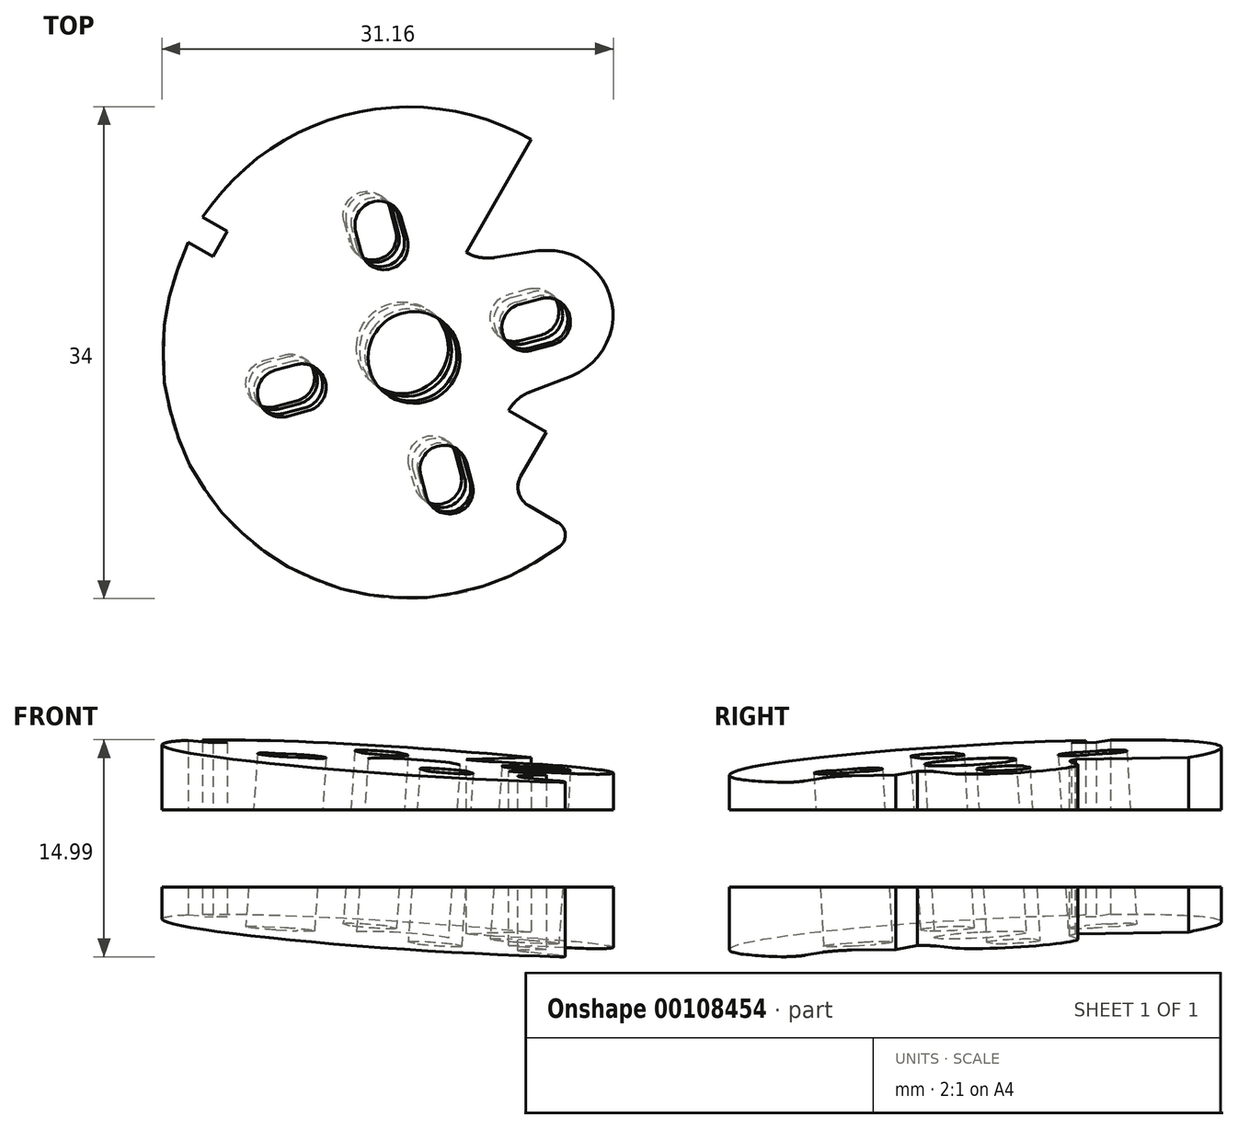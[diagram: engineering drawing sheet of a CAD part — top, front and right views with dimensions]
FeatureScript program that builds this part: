
annotation { "Feature Type Name" : "Feature", "Feature Type Description" : "" }
export const myFeature = defineFeature(function(context is Context, id is Id, definition is map)
    precondition{}
    {
        {
            var Q0;
            Q0=qCreatedBy(makeId("Top.planeOp"),FACE);
            var sketch = newSketch(context, id + "F0", { "sketchPlane" : qUnion([Q0])});
            skCircle(sketch, "E0", {"center": v(0, 0) * mm, "radius": 17 * mm});
            skLineSegment(sketch, "E1", {"start": v(10.93, 13.02) * mm, "end": v(-10.93, -13.02) * mm, "construction": true});
            skSolve(sketch);
        }
        {
            var Q0;
            Q0=qCreatedBy(makeId("Top.planeOp"),FACE);
            var sketch = newSketch(context, id + "F1", { "sketchPlane" : qUnion([Q0])});
            skLineSegment(sketch, "E2", {"start": v(-8.5, -14.72) * mm, "end": v(8.5, 14.72) * mm, "construction": true});
            skPoint(sketch, "E3", {"position": v(0, 0) * mm});
            skLineSegment(sketch, "E4", {"start": v(0, 0) * mm, "end": v(9.18, 2.46) * mm, "construction": true});
            skPoint(sketch, "E5", {"position": v(7.73, 2.07) * mm});
            skArc(sketch, "E6", {"start": v(9.6, 0.91) * mm, "mid": v(10.72, 2.87) * mm, "end": v(8.76, 4) * mm, "construction": true});
            skArc(sketch, "E7", {"start": v(7.31, 3.62) * mm, "mid": v(6.18, 1.66) * mm, "end": v(8.14, 0.53) * mm, "construction": true});
            skLineSegment(sketch, "E8", {"start": v(8.76, 4) * mm, "end": v(7.31, 3.62) * mm, "construction": true});
            skLineSegment(sketch, "E9", {"start": v(9.6, 0.91) * mm, "end": v(8.14, 0.53) * mm, "construction": true});
            skLineSegment(sketch, "E10.1.0", {"start": v(-4, 8.76) * mm, "end": v(-3.62, 7.31) * mm, "construction": true});
            skLineSegment(sketch, "E10.1.1", {"start": v(-0.91, 9.6) * mm, "end": v(-0.53, 8.14) * mm, "construction": true});
            skArc(sketch, "E10.1.2", {"start": v(-3.62, 7.31) * mm, "mid": v(-1.66, 6.18) * mm, "end": v(-0.53, 8.14) * mm, "construction": true});
            skArc(sketch, "E10.1.3", {"start": v(-0.91, 9.6) * mm, "mid": v(-2.87, 10.72) * mm, "end": v(-4, 8.76) * mm, "construction": true});
            skPoint(sketch, "E10.1.4", {"position": v(-2.07, 7.73) * mm});
            skLineSegment(sketch, "E10.2.0", {"start": v(-8.76, -4) * mm, "end": v(-7.31, -3.62) * mm, "construction": true});
            skLineSegment(sketch, "E10.2.1", {"start": v(-9.6, -0.91) * mm, "end": v(-8.14, -0.53) * mm, "construction": true});
            skArc(sketch, "E10.2.2", {"start": v(-7.31, -3.62) * mm, "mid": v(-6.18, -1.66) * mm, "end": v(-8.14, -0.53) * mm, "construction": true});
            skArc(sketch, "E10.2.3", {"start": v(-9.6, -0.91) * mm, "mid": v(-10.72, -2.87) * mm, "end": v(-8.76, -4) * mm, "construction": true});
            skPoint(sketch, "E10.2.4", {"position": v(-7.73, -2.07) * mm});
            skLineSegment(sketch, "E10.3.0", {"start": v(4, -8.76) * mm, "end": v(3.62, -7.31) * mm, "construction": true});
            skLineSegment(sketch, "E10.3.1", {"start": v(0.91, -9.6) * mm, "end": v(0.53, -8.14) * mm, "construction": true});
            skArc(sketch, "E10.3.2", {"start": v(3.62, -7.31) * mm, "mid": v(1.66, -6.18) * mm, "end": v(0.53, -8.14) * mm, "construction": true});
            skArc(sketch, "E10.3.3", {"start": v(0.91, -9.6) * mm, "mid": v(2.87, -10.72) * mm, "end": v(4, -8.76) * mm, "construction": true});
            skPoint(sketch, "E10.3.4", {"position": v(2.07, -7.73) * mm});
            skSolve(sketch);
        }
        {
            var Q0;
            Q0=sQuery(id+"F0.wireOp",EDGE,"E1");
            cPlane(context, id + "F2", {"entities" : qUnion([Q0]), "cplaneType" : CPlaneType.LINE_ANGLE, "offset" : 25 * mm, "angle" : 355 * degree, "width" : 150 * mm, "height" : 150 * mm});
        }
        {
            var Q0;
            Q0=qCreatedBy(id+"F2.planeOp",FACE);
            var sketch = newSketch(context, id + "F3", { "sketchPlane" : qUnion([Q0])});
            skLineSegment(sketch, "E11", {"start": v(0, 0) * mm, "end": v(9.18, -2.44) * mm, "construction": true});
            skPoint(sketch, "E12", {"position": v(7.73, -2.06) * mm});
            skArc(sketch, "E13", {"start": v(8.76, -4.04) * mm, "mid": v(10.78, -2.87) * mm, "end": v(9.6, -0.85) * mm});
            skArc(sketch, "E14", {"start": v(8.16, -0.46) * mm, "mid": v(6.14, -1.63) * mm, "end": v(7.3, -3.65) * mm});
            skLineSegment(sketch, "E15", {"start": v(7.3, -3.65) * mm, "end": v(8.76, -4.04) * mm});
            skLineSegment(sketch, "E16", {"start": v(8.16, -0.46) * mm, "end": v(9.6, -0.85) * mm});
            skCircle(sketch, "E17", {"center": v(0, 0) * mm, "radius": 3.18 * mm});
            skLineSegment(sketch, "E18.1.0", {"start": v(0.46, 8.16) * mm, "end": v(0.85, 9.6) * mm});
            skLineSegment(sketch, "E18.1.1", {"start": v(3.65, 7.31) * mm, "end": v(4.04, 8.76) * mm});
            skArc(sketch, "E18.1.2", {"start": v(0.46, 8.16) * mm, "mid": v(1.63, 6.14) * mm, "end": v(3.65, 7.31) * mm});
            skArc(sketch, "E18.1.3", {"start": v(4.04, 8.76) * mm, "mid": v(2.87, 10.78) * mm, "end": v(0.85, 9.6) * mm});
            skPoint(sketch, "E18.1.4", {"position": v(2.06, 7.73) * mm});
            skLineSegment(sketch, "E18.2.0", {"start": v(-8.16, 0.47) * mm, "end": v(-9.6, 0.85) * mm});
            skLineSegment(sketch, "E18.2.1", {"start": v(-7.3, 3.66) * mm, "end": v(-8.76, 4.04) * mm});
            skArc(sketch, "E18.2.2", {"start": v(-8.16, 0.47) * mm, "mid": v(-6.14, 1.64) * mm, "end": v(-7.3, 3.66) * mm});
            skArc(sketch, "E18.2.3", {"start": v(-8.76, 4.04) * mm, "mid": v(-10.78, 2.87) * mm, "end": v(-9.6, 0.85) * mm});
            skPoint(sketch, "E18.2.4", {"position": v(-7.73, 2.06) * mm});
            skLineSegment(sketch, "E18.3.0", {"start": v(-0.47, -8.15) * mm, "end": v(-0.85, -9.6) * mm});
            skLineSegment(sketch, "E18.3.1", {"start": v(-3.65, -7.3) * mm, "end": v(-4.04, -8.76) * mm});
            skArc(sketch, "E18.3.2", {"start": v(-0.47, -8.15) * mm, "mid": v(-1.64, -6.14) * mm, "end": v(-3.65, -7.3) * mm});
            skArc(sketch, "E18.3.3", {"start": v(-4.04, -8.76) * mm, "mid": v(-2.87, -10.77) * mm, "end": v(-0.85, -9.6) * mm});
            skPoint(sketch, "E18.3.4", {"position": v(-2.06, -7.73) * mm});
            skSolve(sketch);
        }
        {
            var Q0;
            Q0 = qSketchRegion(id + "F0", true);
            extrude(context, id + "F4", {"entities" : qUnion([Q0]), "endBound" : BoundingType.SYMMETRIC, "depth" : 25 * mm});
        }
        {
            var Q0;
            Q0 = qSketchRegion(id + "F3", true);
            extrude(context, id + "F5", {"entities" : qUnion([Q0]), "operationType" : NewBodyOperationType.REMOVE, "endBound" : BoundingType.THROUGH_ALL, "oppositeDirection" : true, "depth" : 25 * mm, "hasSecondDirection" : true, "secondDirectionBound" : SecondDirectionBoundingType.THROUGH_ALL, "secondDirectionOppositeDirection" : false, "secondDirectionDepth" : 25 * mm});
        }
        {
            var Q0;
            Q0=qCreatedBy(id+"F2.planeOp",FACE);
            cPlane(context, id + "F6", {"entities" : qUnion([Q0]), "cplaneType" : CPlaneType.OFFSET, "offset" : 6 * mm, "oppositeDirection" : true, "width" : 150 * mm, "height" : 150 * mm});
        }
        {
            var Q0;
            Q0=qCreatedBy(id+"F2.planeOp",FACE);
            cPlane(context, id + "F7", {"entities" : qUnion([Q0]), "cplaneType" : CPlaneType.OFFSET, "offset" : 6 * mm, "width" : 150 * mm, "height" : 150 * mm});
        }
        {
            var Q0;
            Q0=qCreatedBy(id+"F6.planeOp",FACE);
            var sketch = newSketch(context, id + "F8", { "sketchPlane" : qUnion([Q0])});
            skCircle(sketch, "E19", {"center": v(0, 0) * mm, "radius": 20 * mm});
            skSolve(sketch);
        }
        {
            var Q0;
            Q0 = qSketchRegion(id + "F8", true);
            var Q1;
            Q1=makeQuery(id+"F4.opExtrude","CAP_FACE",FACE,{"disambiguationData":[OSD([sQuery(id+"F0.wireOp",EDGE,"E0")])],"isStart":false});
            extrude(context, id + "F9", {"entities" : qUnion([Q0]), "operationType" : NewBodyOperationType.REMOVE, "endBound" : BoundingType.UP_TO_SURFACE, "oppositeDirection" : true, "endBoundEntityFace" : qUnion([Q1]), "depth" : 25 * mm});
        }
        {
            var Q0;
            Q0=qCreatedBy(id+"F7.planeOp",FACE);
            var sketch = newSketch(context, id + "F10", { "sketchPlane" : qUnion([Q0])});
            skCircle(sketch, "E20", {"center": v(0, 0) * mm, "radius": 20 * mm});
            skSolve(sketch);
        }
        {
            var Q0;
            Q0 = qSketchRegion(id + "F10", true);
            var Q1;
            Q1=makeQuery(id+"F4.opExtrude","CAP_FACE",FACE,{"disambiguationData":[OSD([sQuery(id+"F0.wireOp",EDGE,"E0")])],"isStart":true});
            extrude(context, id + "F11", {"entities" : qUnion([Q0]), "operationType" : NewBodyOperationType.REMOVE, "endBound" : BoundingType.UP_TO_SURFACE, "endBoundEntityFace" : qUnion([Q1]), "depth" : 25 * mm});
        }
        {
            var Q0;
            Q0=qCreatedBy(makeId("Front.planeOp"),FACE);
            var sketch = newSketch(context, id + "F12", { "sketchPlane" : qUnion([Q0])});
            skLineSegment(sketch, "E21.bottom", {"start": v(20, 2.67) * mm, "end": v(-20, 2.67) * mm});
            skLineSegment(sketch, "E21.top", {"start": v(20, -2.67) * mm, "end": v(-20, -2.67) * mm});
            skLineSegment(sketch, "E21.left", {"start": v(20, 2.67) * mm, "end": v(20, -2.67) * mm});
            skLineSegment(sketch, "E21.right", {"start": v(-20, 2.67) * mm, "end": v(-20, -2.67) * mm});
            skPoint(sketch, "E21.middle", {"position": v(0, 0) * mm});
            skSolve(sketch);
        }
        {
            var Q0;
            Q0 = qSketchRegion(id + "F12", true);
            extrude(context, id + "F13", {"entities" : qUnion([Q0]), "operationType" : NewBodyOperationType.REMOVE, "endBound" : BoundingType.THROUGH_ALL, "oppositeDirection" : true, "depth" : 25 * mm, "hasSecondDirection" : true, "secondDirectionBound" : SecondDirectionBoundingType.THROUGH_ALL, "secondDirectionOppositeDirection" : false, "secondDirectionDepth" : 25 * mm});
        }
        {
            var Q0;
            Q0=sQuery(id+"F1.wireOp",EDGE,"E2");
            cPlane(context, id + "F14", {"entities" : qUnion([Q0]), "cplaneType" : CPlaneType.LINE_ANGLE, "offset" : 25 * mm, "angle" : 90 * degree, "width" : 150 * mm, "height" : 150 * mm});
        }
        {
            var Q0;
            Q0=qCreatedBy(id+"F14.planeOp",FACE);
            cPlane(context, id + "F15", {"entities" : qUnion([Q0]), "cplaneType" : CPlaneType.OFFSET, "offset" : 17 * mm, "width" : 150 * mm, "height" : 150 * mm});
        }
        {
            var Q0;
            Q0=qCreatedBy(id+"F14.planeOp",FACE);
            cPlane(context, id + "F16", {"entities" : qUnion([Q0]), "cplaneType" : CPlaneType.OFFSET, "offset" : 17 * mm, "oppositeDirection" : true, "width" : 150 * mm, "height" : 150 * mm});
        }
        {
            var Q0;
            Q0=qCreatedBy(id+"F15.planeOp",FACE);
            var sketch = newSketch(context, id + "F17", { "sketchPlane" : qUnion([Q0])});
            skLineSegment(sketch, "E22.bottom", {"start": v(1, 12.5) * mm, "end": v(-1, 12.5) * mm});
            skLineSegment(sketch, "E22.top", {"start": v(1, -12.5) * mm, "end": v(-1, -12.5) * mm});
            skLineSegment(sketch, "E22.left", {"start": v(1, 12.5) * mm, "end": v(1, -12.5) * mm});
            skLineSegment(sketch, "E22.right", {"start": v(-1, 12.5) * mm, "end": v(-1, -12.5) * mm});
            skPoint(sketch, "E22.middle", {"position": v(0, 0) * mm});
            skSolve(sketch);
        }
        {
            var Q0;
            Q0 = qSketchRegion(id + "F17", true);
            extrude(context, id + "F18", {"entities" : qUnion([Q0]), "operationType" : NewBodyOperationType.REMOVE, "oppositeDirection" : true, "depth" : 2 * mm});
        }
        {
            var Q0;
            Q0=qCreatedBy(id+"F16.planeOp",FACE);
            var sketch = newSketch(context, id + "F19", { "sketchPlane" : qUnion([Q0])});
            skLineSegment(sketch, "E23.0", {"start": v(-1, 12.5) * mm, "end": v(-1, -12.5) * mm});
            skLineSegment(sketch, "E23.1", {"start": v(1, 12.5) * mm, "end": v(-1, 12.5) * mm});
            skLineSegment(sketch, "E23.2", {"start": v(1, 12.5) * mm, "end": v(1, -12.5) * mm});
            skLineSegment(sketch, "E23.3", {"start": v(1, -12.5) * mm, "end": v(-1, -12.5) * mm});
            skSolve(sketch);
        }
        {
            var Q0;
            Q0 = qSketchRegion(id + "F19", true);
            extrude(context, id + "F20", {"entities" : qUnion([Q0]), "operationType" : NewBodyOperationType.REMOVE, "depth" : 2 * mm});
        }
        {
            var Q0;
            Q0=qCreatedBy(makeId("Top.planeOp"),FACE);
            var sketch = newSketch(context, id + "F21", { "sketchPlane" : qUnion([Q0])});
            skLineSegment(sketch, "E24", {"start": v(0, 0) * mm, "end": v(28.57, -16.5) * mm, "construction": true});
            skLineSegment(sketch, "E25.0", {"start": v(8.33, -10.58) * mm, "end": v(13.09, -13.33) * mm});
            skLineSegment(sketch, "E26.0", {"start": v(13.33, -1.92) * mm, "end": v(18.09, -4.67) * mm});
            skLineSegment(sketch, "E27", {"start": v(7.78, -8.53) * mm, "end": v(11.28, -2.47) * mm});
            skLineSegment(sketch, "E28", {"start": v(13.09, -13.33) * mm, "end": v(18.09, -4.67) * mm});
            skPoint(sketch, "E29.visualSharp", {"position": v(7.03, -9.83) * mm});
            skArc(sketch, "E29.filletArc", {"start": v(7.78, -8.53) * mm, "mid": v(7.63, -9.67) * mm, "end": v(8.33, -10.58) * mm});
            skPoint(sketch, "E30.visualSharp", {"position": v(12.03, -1.17) * mm});
            skArc(sketch, "E30.filletArc", {"start": v(13.33, -1.92) * mm, "mid": v(12.19, -1.77) * mm, "end": v(11.28, -2.47) * mm});
            skSolve(sketch);
        }
        {
            var Q0;
            Q0 = qSketchRegion(id + "F21", true);
            extrude(context, id + "F22", {"entities" : qUnion([Q0]), "operationType" : NewBodyOperationType.REMOVE, "endBound" : BoundingType.THROUGH_ALL, "oppositeDirection" : true, "depth" : 25 * mm, "hasSecondDirection" : true, "secondDirectionBound" : SecondDirectionBoundingType.THROUGH_ALL, "secondDirectionOppositeDirection" : false, "secondDirectionDepth" : 25 * mm});
        }
        {
            var Q0;
            {var subQ0=makeQuery(id+"F9.boolean.opBoolean","COPY",FACE,{"derivedFrom":makeQuery(id+"F9.opExtrude","CAP_FACE",FACE,{"disambiguationData":[OSD([sQuery(id+"F8.wireOp",EDGE,"E19")])],"isStart":true})});Q0=makeQuery(id+"F22.boolean.opBoolean","INTERSECT",EDGE,{"derivedFrom":[makeQuery(id+"F20.boolean.opBoolean","SPLIT",FACE,{"disambiguationData":[TD([makeQuery(id+"F18.boolean.opBoolean","COPY",FACE,{"disambiguationData":[OD(0.0)],"derivedFrom":makeQuery(id+"F18.opExtrude","SWEPT_FACE",FACE,{"disambiguationData":[OSD([sQuery(id+"F17.wireOp",EDGE,"E22.right")])]})})])],"derivedFrom":makeQuery(id+"F13.boolean.opBoolean","SPLIT",FACE,{"disambiguationData":[TD([subQ0])],"derivedFrom":makeQuery(id+"F4.opExtrude","SWEPT_FACE",FACE,{"disambiguationData":[OSD([sQuery(id+"F0.wireOp",EDGE,"E0")])]})})}),makeQuery(id+"F22.opExtrude","SWEPT_FACE",FACE,{"disambiguationData":[OSD([sQuery(id+"F21.wireOp",EDGE,"E25.0")])]})]});}
            var Q1;
            {var subQ0=makeQuery(id+"F9.boolean.opBoolean","COPY",FACE,{"derivedFrom":makeQuery(id+"F9.opExtrude","CAP_FACE",FACE,{"disambiguationData":[OSD([sQuery(id+"F8.wireOp",EDGE,"E19")])],"isStart":true})});Q1=makeQuery(id+"F22.boolean.opBoolean","INTERSECT",EDGE,{"derivedFrom":[makeQuery(id+"F20.boolean.opBoolean","SPLIT",FACE,{"disambiguationData":[TD([makeQuery(id+"F18.boolean.opBoolean","COPY",FACE,{"disambiguationData":[OD(0.0)],"derivedFrom":makeQuery(id+"F18.opExtrude","SWEPT_FACE",FACE,{"disambiguationData":[OSD([sQuery(id+"F17.wireOp",EDGE,"E22.left")])]})})])],"derivedFrom":makeQuery(id+"F13.boolean.opBoolean","SPLIT",FACE,{"disambiguationData":[TD([subQ0])],"derivedFrom":makeQuery(id+"F4.opExtrude","SWEPT_FACE",FACE,{"disambiguationData":[OSD([sQuery(id+"F0.wireOp",EDGE,"E0")])]})})}),makeQuery(id+"F22.opExtrude","SWEPT_FACE",FACE,{"disambiguationData":[OSD([sQuery(id+"F21.wireOp",EDGE,"E26.0")])]})]});}
            var Q2;
            {var subQ0=makeQuery(id+"F11.boolean.opBoolean","COPY",FACE,{"derivedFrom":makeQuery(id+"F11.opExtrude","CAP_FACE",FACE,{"disambiguationData":[OSD([sQuery(id+"F10.wireOp",EDGE,"E20")])],"isStart":true})});Q2=makeQuery(id+"F22.boolean.opBoolean","INTERSECT",EDGE,{"derivedFrom":[makeQuery(id+"F20.boolean.opBoolean","SPLIT",FACE,{"disambiguationData":[TD([makeQuery(id+"F18.boolean.opBoolean","COPY",FACE,{"disambiguationData":[OD(1.0)],"derivedFrom":makeQuery(id+"F18.opExtrude","SWEPT_FACE",FACE,{"disambiguationData":[OSD([sQuery(id+"F17.wireOp",EDGE,"E22.right")])]})})])],"derivedFrom":makeQuery(id+"F13.boolean.opBoolean","SPLIT",FACE,{"disambiguationData":[TD([subQ0])],"derivedFrom":makeQuery(id+"F4.opExtrude","SWEPT_FACE",FACE,{"disambiguationData":[OSD([sQuery(id+"F0.wireOp",EDGE,"E0")])]})})}),makeQuery(id+"F22.opExtrude","SWEPT_FACE",FACE,{"disambiguationData":[OSD([sQuery(id+"F21.wireOp",EDGE,"E25.0")])]})]});}
            var Q3;
            {var subQ0=makeQuery(id+"F11.boolean.opBoolean","COPY",FACE,{"derivedFrom":makeQuery(id+"F11.opExtrude","CAP_FACE",FACE,{"disambiguationData":[OSD([sQuery(id+"F10.wireOp",EDGE,"E20")])],"isStart":true})});Q3=makeQuery(id+"F22.boolean.opBoolean","INTERSECT",EDGE,{"derivedFrom":[makeQuery(id+"F20.boolean.opBoolean","SPLIT",FACE,{"disambiguationData":[TD([makeQuery(id+"F18.boolean.opBoolean","COPY",FACE,{"disambiguationData":[OD(1.0)],"derivedFrom":makeQuery(id+"F18.opExtrude","SWEPT_FACE",FACE,{"disambiguationData":[OSD([sQuery(id+"F17.wireOp",EDGE,"E22.left")])]})})])],"derivedFrom":makeQuery(id+"F13.boolean.opBoolean","SPLIT",FACE,{"disambiguationData":[TD([subQ0])],"derivedFrom":makeQuery(id+"F4.opExtrude","SWEPT_FACE",FACE,{"disambiguationData":[OSD([sQuery(id+"F0.wireOp",EDGE,"E0")])]})})}),makeQuery(id+"F22.opExtrude","SWEPT_FACE",FACE,{"disambiguationData":[OSD([sQuery(id+"F21.wireOp",EDGE,"E26.0")])]})]});}
            fillet(context, id + "F23", {"entities" : qUnion([Q0, Q1, Q2, Q3]), "radius" : 1 * mm, "tangentPropagation" : true, "allowEdgeOverflow" : false});
        }
        {
            var Q0;
            Q0=qCreatedBy(makeId("Top.planeOp"),FACE);
            var sketch = newSketch(context, id + "F24", { "sketchPlane" : qUnion([Q0])});
            skLineSegment(sketch, "E31", {"start": v(0, 0) * mm, "end": v(9.53, -5.5) * mm, "construction": true});
            skLineSegment(sketch, "E32", {"start": v(0, 0) * mm, "end": v(5.5, 9.53) * mm, "construction": true});
            skArc(sketch, "E33.0", {"start": v(16.45, -9.5) * mm, "mid": v(18.35, 4.92) * mm, "end": v(9.5, 16.45) * mm});
            skArc(sketch, "E34", {"start": v(4, 6.93) * mm, "mid": v(4.95, 6.58) * mm, "end": v(5.97, 6.56) * mm});
            skArc(sketch, "E35", {"start": v(8.45, -2.7) * mm, "mid": v(7.58, -3.22) * mm, "end": v(6.93, -4) * mm});
            skLineSegment(sketch, "E36", {"start": v(0, 0) * mm, "end": v(9.66, 2.59) * mm, "construction": true});
            skArc(sketch, "E37", {"start": v(11.28, -1.61) * mm, "mid": v(14, 3.75) * mm, "end": v(8.96, 7.03) * mm});
            skLineSegment(sketch, "E38", {"start": v(5.97, 6.56) * mm, "end": v(8.96, 7.03) * mm});
            skLineSegment(sketch, "E39", {"start": v(8.45, -2.7) * mm, "end": v(11.28, -1.61) * mm});
            skLineSegment(sketch, "E40", {"start": v(6.93, -4) * mm, "end": v(16.45, -9.5) * mm});
            skLineSegment(sketch, "E41", {"start": v(4, 6.93) * mm, "end": v(9.5, 16.45) * mm});
            skSolve(sketch);
        }
        {
            var Q0;
            Q0 = qSketchRegion(id + "F24", true);
            extrude(context, id + "F25", {"entities" : qUnion([Q0]), "operationType" : NewBodyOperationType.REMOVE, "endBound" : BoundingType.THROUGH_ALL, "oppositeDirection" : true, "depth" : 25 * mm, "hasSecondDirection" : true, "secondDirectionBound" : SecondDirectionBoundingType.THROUGH_ALL, "secondDirectionOppositeDirection" : false, "secondDirectionDepth" : 25 * mm});
        }
        {
            var Q0;
            Q0=qCreatedBy(makeId("Front.planeOp"),FACE);
            var sketch = newSketch(context, id + "F26", { "sketchPlane" : qUnion([Q0])});
            skLineSegment(sketch, "E42", {"start": v(0, 0) * mm, "end": v(0, 59.66) * mm, "construction": true});
            skSolve(sketch);
        }
    });
